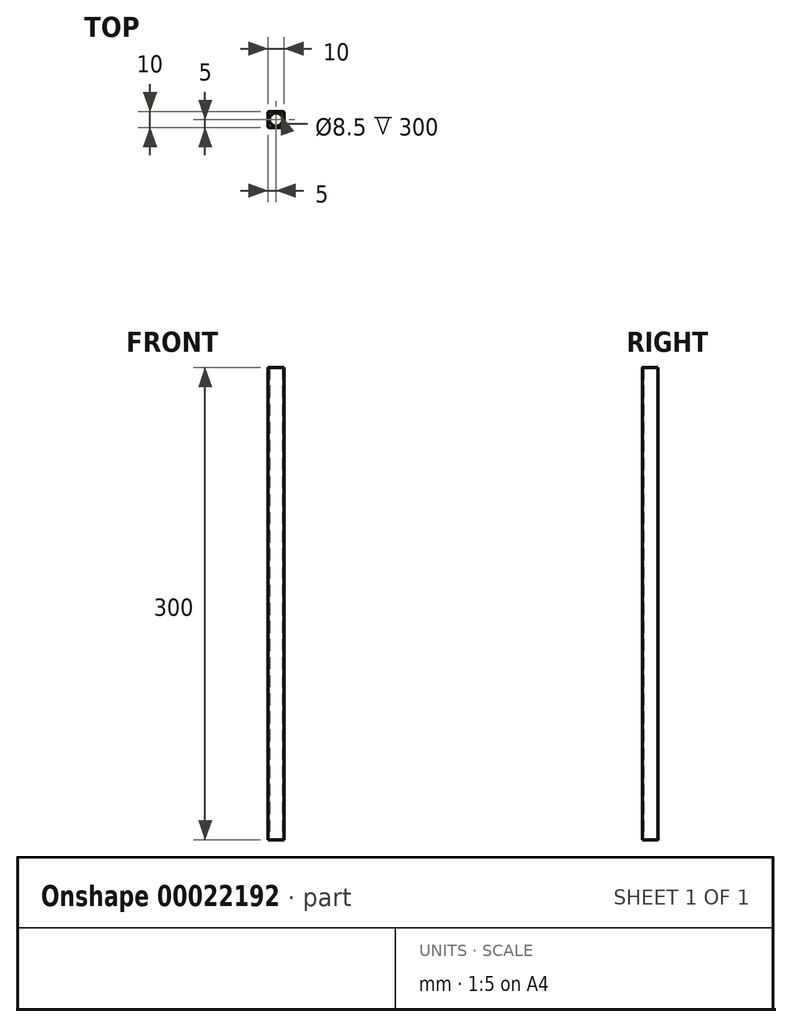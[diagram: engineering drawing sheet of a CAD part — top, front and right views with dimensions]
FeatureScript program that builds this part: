
annotation { "Feature Type Name" : "Feature", "Feature Type Description" : "" }
export const myFeature = defineFeature(function(context is Context, id is Id, definition is map)
    precondition{}
    {
        {
            var Q0;
            Q0=qCreatedBy(makeId("Top.planeOp"),FACE);
            var sketch = newSketch(context, id + "F0", { "sketchPlane" : qUnion([Q0])});
            skCircle(sketch, "E0", {"center": v(0, 0) * mm, "radius": 4.25 * mm});
            skLineSegment(sketch, "E1.rect.bottom", {"start": v(4.5, 5) * mm, "end": v(-4.5, 5) * mm});
            skLineSegment(sketch, "E1.rect.top", {"start": v(4.5, -5) * mm, "end": v(-4.5, -5) * mm});
            skLineSegment(sketch, "E1.rect.left", {"start": v(5, 4.5) * mm, "end": v(5, -4.5) * mm});
            skLineSegment(sketch, "E1.rect.right", {"start": v(-5, 4.5) * mm, "end": v(-5, -4.5) * mm});
            skPoint(sketch, "E2.visualSharp", {"position": v(-5, 5) * mm});
            skArc(sketch, "E2.filletArc", {"start": v(-4.5, 5) * mm, "mid": v(-4.85, 4.85) * mm, "end": v(-5, 4.5) * mm});
            skPoint(sketch, "E3.visualSharp", {"position": v(5, 5) * mm});
            skArc(sketch, "E3.filletArc", {"start": v(5, 4.5) * mm, "mid": v(4.85, 4.85) * mm, "end": v(4.5, 5) * mm});
            skPoint(sketch, "E4.visualSharp", {"position": v(5, -5) * mm});
            skArc(sketch, "E4.filletArc", {"start": v(4.5, -5) * mm, "mid": v(4.85, -4.85) * mm, "end": v(5, -4.5) * mm});
            skPoint(sketch, "E5.visualSharp", {"position": v(-5, -5) * mm});
            skArc(sketch, "E5.filletArc", {"start": v(-5, -4.5) * mm, "mid": v(-4.85, -4.85) * mm, "end": v(-4.5, -5) * mm});
            skSolve(sketch);
        }
        {
            var Q0;
            Q0 = qSketchRegion(id + "F0", true);
            extrude(context, id + "F1", {"entities" : qUnion([Q0]), "depth" : 300 * mm});
        }
    });
